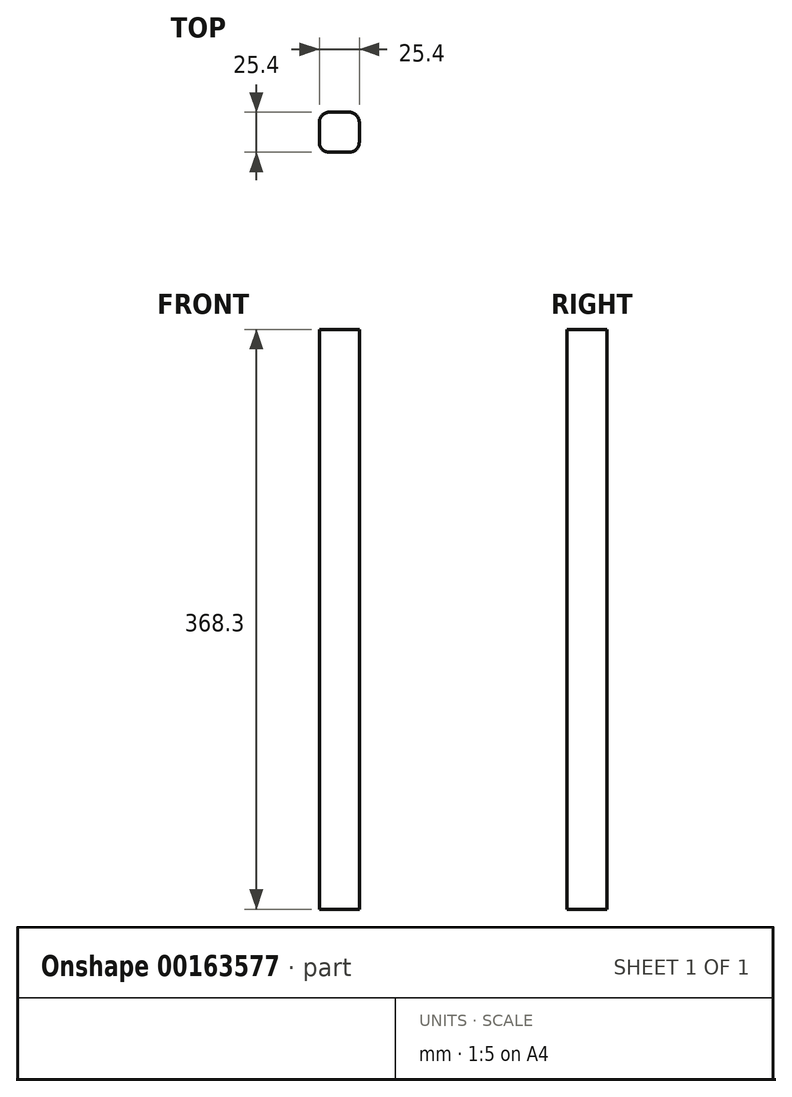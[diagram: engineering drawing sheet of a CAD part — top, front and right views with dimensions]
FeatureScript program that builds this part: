
annotation { "Feature Type Name" : "Feature", "Feature Type Description" : "" }
export const myFeature = defineFeature(function(context is Context, id is Id, definition is map)
    precondition{}
    {
        {
            var Q0;
            Q0=qCreatedBy(makeId("Top.planeOp"),FACE);
            var sketch = newSketch(context, id + "F0", { "sketchPlane" : qUnion([Q0])});
            skLineSegment(sketch, "E0.bottom", {"start": v(6.35, 12.7) * mm, "end": v(-6.35, 12.7) * mm});
            skLineSegment(sketch, "E0.top", {"start": v(6.35, -12.7) * mm, "end": v(-6.35, -12.7) * mm});
            skLineSegment(sketch, "E0.left", {"start": v(12.7, 6.35) * mm, "end": v(12.7, -6.35) * mm});
            skLineSegment(sketch, "E0.right", {"start": v(-12.7, 6.35) * mm, "end": v(-12.7, -6.35) * mm});
            skPoint(sketch, "E0.middle", {"position": v(0, 0) * mm});
            skPoint(sketch, "E1.visualSharp", {"position": v(-12.7, 12.7) * mm});
            skArc(sketch, "E1.filletArc", {"start": v(-6.35, 12.7) * mm, "mid": v(-10.84, 10.84) * mm, "end": v(-12.7, 6.35) * mm});
            skPoint(sketch, "E2.visualSharp", {"position": v(-12.7, -12.7) * mm});
            skArc(sketch, "E2.filletArc", {"start": v(-12.7, -6.35) * mm, "mid": v(-10.84, -10.84) * mm, "end": v(-6.35, -12.7) * mm});
            skPoint(sketch, "E3.visualSharp", {"position": v(12.7, -12.7) * mm});
            skArc(sketch, "E3.filletArc", {"start": v(6.35, -12.7) * mm, "mid": v(10.84, -10.84) * mm, "end": v(12.7, -6.35) * mm});
            skPoint(sketch, "E4.visualSharp", {"position": v(12.7, 12.7) * mm});
            skArc(sketch, "E4.filletArc", {"start": v(12.7, 6.35) * mm, "mid": v(10.84, 10.84) * mm, "end": v(6.35, 12.7) * mm});
            skSolve(sketch);
        }
        {
            var Q0;
            Q0=qSketchRegion(id+"F0",true);
            extrude(context, id + "F1", {"entities" : qUnion([Q0]), "depth" : 368.3 * mm, "offsetDistance" : 25.4 * mm});
        }
    });
